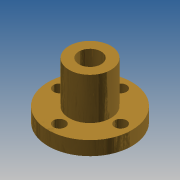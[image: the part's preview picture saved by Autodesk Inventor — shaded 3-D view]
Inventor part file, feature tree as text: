
AUTODESK INVENTOR PART (.ipt)
format: ipt  version: 2013 (Build 170138000, 138)  size: 107,520 bytes
history: native  units: mm
features: extrude x4, sketch x4, pattern_circular x1
ambient origin geometry x8: Origin, YZ Plane, XZ Plane, XY Plane, X Axis, Y Axis, Z Axis, Center Point
bodies: Solid1 (feature_tree)
feature tree (9):
  extrude  "Extrusion1"  Depth=5.0mm TaperAngle=0.0deg
  extrude  "Extrusion2"  Depth=15.0mm TaperAngle=0.0deg
  extrude  "Extrusion3"  Depth=15.0mm TaperAngle=0.0deg
  extrude  "Extrusion4"  Depth=4.3mm
  pattern_circular  "Circular Pattern1"  [2 undecoded]
  sketch  "Sketch1"  dims[d0=30.0mm d2=5.0mm d3=0.0mm]
  sketch  "Sketch2"  dims[d4=15.0mm d6=15.0mm d7=0.0mm]
  sketch  "Sketch3"  dims[d8=8.0mm d11=15.0mm d12=0.0mm]
  sketch  "Sketch4"  dims[d13=11.0mm d14=4.3mm d15=15.0mm d16=0.0mm d17=40.0mm d18=360.0deg]
note: 2 required parameter values undecoded (feature->parameter linkage not recoverable at this tier; creation-order binding heuristic only, values carry confidence <= 0.55)
